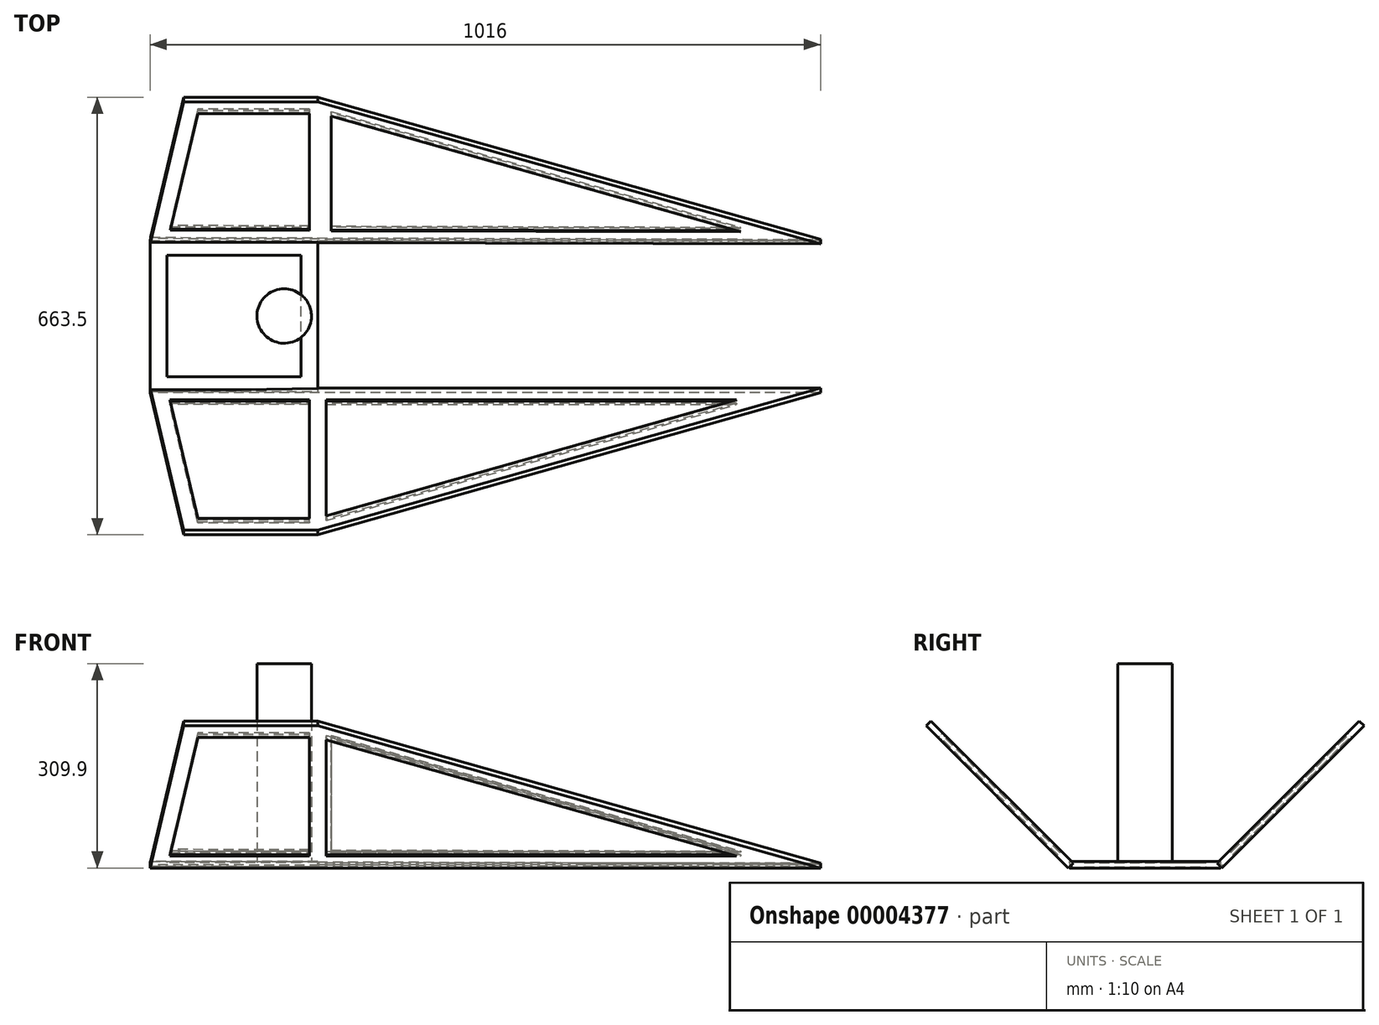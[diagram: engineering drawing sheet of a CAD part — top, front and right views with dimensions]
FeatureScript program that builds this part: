
annotation { "Feature Type Name" : "Feature", "Feature Type Description" : "" }
export const myFeature = defineFeature(function(context is Context, id is Id, definition is map)
    precondition{}
    {
        {
            var Q0;
            Q0=qCreatedBy(makeId("Top.planeOp"),FACE);
            var sketch = newSketch(context, id + "F0", { "sketchPlane" : qUnion([Q0])});
            skLineSegment(sketch, "E0.rect.bottom", {"start": v(-127, 114.3) * mm, "end": v(127, 114.3) * mm});
            skLineSegment(sketch, "E0.rect.top", {"start": v(-127, -114.3) * mm, "end": v(127, -114.3) * mm});
            skLineSegment(sketch, "E0.rect.left", {"start": v(-127, 114.3) * mm, "end": v(-127, -114.3) * mm});
            skLineSegment(sketch, "E0.rect.right", {"start": v(127, 114.3) * mm, "end": v(127, -114.3) * mm});
            skPoint(sketch, "E0.rect.middle", {"position": v(0, 0) * mm});
            skSolve(sketch);
        }
        {
            var Q0;
            Q0=makeQuery(id+"F0.imprint","IMPRINT",FACE,{"disambiguationData":[TD([[makeQuery(id+"F0.imprint","IMPRINT",EDGE,{"derivedFrom":sQuery(id+"F0.wireOp",EDGE,"E0.rect.bottom")}),-1.0]])]});
            extrude(context, id + "F1", {"entities" : qUnion([Q0]), "endBound" : BoundingType.SYMMETRIC, "depth" : 6.35 * mm});
        }
        {
            var Q0;
            Q0=makeQuery(id+"F1.opExtrude","CAP_EDGE",EDGE,{"disambiguationData":[OSD([sQuery(id+"F0.wireOp",EDGE,"E0.rect.top")])],"isStart":true});
            cPlane(context, id + "F2", {"entities" : qUnion([Q0]), "cplaneType" : CPlaneType.LINE_ANGLE, "offset" : 152.4 * mm, "angle" : 45 * degree, "width" : 152.4 * mm, "height" : 152.4 * mm});
        }
        {
            var Q0;
            Q0=qCreatedBy(id+"F2.planeOp",FACE);
            var sketch = newSketch(context, id + "F3", { "sketchPlane" : qUnion([Q0])});
            skLineSegment(sketch, "E1.0", {"start": v(127, 78.58) * mm, "end": v(-127, 78.58) * mm});
            skLineSegment(sketch, "E2", {"start": v(-127, 78.58) * mm, "end": v(-127, 383.38) * mm});
            skLineSegment(sketch, "E3", {"start": v(-127, 383.38) * mm, "end": v(76.2, 383.38) * mm});
            skLineSegment(sketch, "E4", {"start": v(127, 78.58) * mm, "end": v(76.2, 383.38) * mm});
            skSolve(sketch);
        }
        {
            var Q0;
            Q0=makeQuery(id+"F3.imprint","IMPRINT",FACE,{"disambiguationData":[TD([[makeQuery(id+"F3.imprint","IMPRINT",EDGE,{"derivedFrom":sQuery(id+"F3.wireOp",EDGE,"E1.0")}),-1.0]])]});
            extrude(context, id + "F4", {"entities" : qUnion([Q0]), "operationType" : NewBodyOperationType.ADD, "depth" : 4.72 * mm});
        }
        {
            var Q0;
            Q0=makeQuery(id+"F1.opExtrude","CAP_EDGE",EDGE,{"disambiguationData":[OSD([sQuery(id+"F0.wireOp",EDGE,"E0.rect.bottom")])],"isStart":true});
            cPlane(context, id + "F5", {"entities" : qUnion([Q0]), "cplaneType" : CPlaneType.LINE_ANGLE, "offset" : 152.4 * mm, "angle" : 135 * degree, "width" : 152.4 * mm, "height" : 152.4 * mm});
        }
        {
            var Q0;
            Q0=qCreatedBy(id+"F5.planeOp",FACE);
            var sketch = newSketch(context, id + "F6", { "sketchPlane" : qUnion([Q0])});
            skLineSegment(sketch, "E5.0", {"start": v(-127, 78.58) * mm, "end": v(127, 78.58) * mm});
            skLineSegment(sketch, "E6", {"start": v(127, 78.58) * mm, "end": v(127, 383.38) * mm});
            skLineSegment(sketch, "E7.0", {"start": v(127, -83.07) * mm, "end": v(-76.2, -83.07) * mm, "construction": true});
            skLineSegment(sketch, "E8", {"start": v(127, 383.38) * mm, "end": v(-76.2, 383.38) * mm});
            skLineSegment(sketch, "E9", {"start": v(-76.2, 383.38) * mm, "end": v(-127, 78.58) * mm});
            skSolve(sketch);
        }
        {
            var Q0;
            Q0=makeQuery(id+"F6.imprint","IMPRINT",FACE,{"disambiguationData":[TD([[makeQuery(id+"F6.imprint","IMPRINT",EDGE,{"derivedFrom":sQuery(id+"F6.wireOp",EDGE,"E5.0")}),1.0]])]});
            extrude(context, id + "F7", {"entities" : qUnion([Q0]), "operationType" : NewBodyOperationType.ADD, "depth" : 4.72 * mm});
        }
        {
            var Q0;
            Q0=qCreatedBy(id+"F2.planeOp",FACE);
            var sketch = newSketch(context, id + "F8", { "sketchPlane" : qUnion([Q0])});
            skLineSegment(sketch, "E10.0", {"start": v(-127, 78.58) * mm, "end": v(-127, 383.38) * mm});
            skLineSegment(sketch, "E11", {"start": v(-127, 78.58) * mm, "end": v(-889, 78.58) * mm});
            skLineSegment(sketch, "E12", {"start": v(-889, 78.58) * mm, "end": v(-127, 383.38) * mm});
            skSolve(sketch);
        }
        {
            var Q0;
            Q0=makeQuery(id+"F8.imprint","IMPRINT",FACE,{"disambiguationData":[TD([[makeQuery(id+"F8.imprint","IMPRINT",EDGE,{"derivedFrom":sQuery(id+"F8.wireOp",EDGE,"E10.0")}),1.0]])]});
            extrude(context, id + "F9", {"entities" : qUnion([Q0]), "operationType" : NewBodyOperationType.ADD, "depth" : 4.72 * mm});
        }
        {
            var Q0;
            Q0=qCreatedBy(id+"F5.planeOp",FACE);
            var sketch = newSketch(context, id + "F10", { "sketchPlane" : qUnion([Q0])});
            skLineSegment(sketch, "E13.0", {"start": v(127, 78.58) * mm, "end": v(127, 383.38) * mm});
            skLineSegment(sketch, "E14", {"start": v(127, 78.58) * mm, "end": v(889, 78.58) * mm});
            skLineSegment(sketch, "E15", {"start": v(889, 78.58) * mm, "end": v(127, 383.38) * mm});
            skSolve(sketch);
        }
        {
            var Q0;
            Q0=makeQuery(id+"F10.imprint","IMPRINT",FACE,{"disambiguationData":[TD([[makeQuery(id+"F10.imprint","IMPRINT",EDGE,{"derivedFrom":sQuery(id+"F10.wireOp",EDGE,"E13.0")}),-1.0]])]});
            extrude(context, id + "F11", {"entities" : qUnion([Q0]), "operationType" : NewBodyOperationType.ADD, "depth" : 4.72 * mm});
        }
        {
            var Q0;
            Q0=makeQuery(id+"F9.boolean.opBoolean","MERGE",FACE,{"derivedFrom":[makeQuery(id+"F4.opExtrude","CAP_FACE",FACE,{"disambiguationData":[OSD([sQuery(id+"F3.wireOp",EDGE,"E1.0"),sQuery(id+"F3.wireOp",EDGE,"E2"),sQuery(id+"F3.wireOp",EDGE,"E3"),sQuery(id+"F3.wireOp",EDGE,"E4")])],"isStart":false}),makeQuery(id+"F9.opExtrude","CAP_FACE",FACE,{"disambiguationData":[OSD([sQuery(id+"F8.wireOp",EDGE,"E10.0"),sQuery(id+"F8.wireOp",EDGE,"E11"),sQuery(id+"F8.wireOp",EDGE,"E12")])],"isStart":false})]});
            cPlane(context, id + "F12", {"entities" : qUnion([Q0]), "cplaneType" : CPlaneType.OFFSET, "offset" : 2.36 * mm, "oppositeDirection" : true, "width" : 152.4 * mm, "height" : 152.4 * mm});
        }
        {
            var Q0;
            Q0=qCreatedBy(id+"F12.planeOp",FACE);
            var sketch = newSketch(context, id + "F13", { "sketchPlane" : qUnion([Q0])});
            skLineSegment(sketch, "E16.0", {"start": v(-889, 78.58) * mm, "end": v(-127, 383.38) * mm});
            skLineSegment(sketch, "E17.0", {"start": v(-127, 383.38) * mm, "end": v(76.2, 383.38) * mm});
            skLineSegment(sketch, "E18.0", {"start": v(127, 78.58) * mm, "end": v(76.2, 383.38) * mm});
            skLineSegment(sketch, "E19", {"start": v(-889, 78.58) * mm, "end": v(127, 78.58) * mm});
            skLineSegment(sketch, "E20", {"start": v(-139.7, 352.8) * mm, "end": v(-761.76, 103.98) * mm});
            skLineSegment(sketch, "E21", {"start": v(-139.7, 103.98) * mm, "end": v(-761.76, 103.98) * mm});
            skLineSegment(sketch, "E22", {"start": v(-114.3, 357.98) * mm, "end": v(54.68, 357.98) * mm});
            skLineSegment(sketch, "E23", {"start": v(54.68, 357.98) * mm, "end": v(97.02, 103.98) * mm});
            skLineSegment(sketch, "E24", {"start": v(-114.3, 103.98) * mm, "end": v(97.02, 103.98) * mm});
            skLineSegment(sketch, "E25", {"start": v(-114.3, 357.98) * mm, "end": v(-114.3, 103.98) * mm});
            skLineSegment(sketch, "E26", {"start": v(-139.7, 352.8) * mm, "end": v(-139.7, 103.98) * mm});
            skSolve(sketch);
        }
        {
            var Q0;
            Q0=makeQuery(id+"F13.imprint","IMPRINT",FACE,{"disambiguationData":[TD([[makeQuery(id+"F13.imprint","IMPRINT",EDGE,{"derivedFrom":sQuery(id+"F13.wireOp",EDGE,"E16.0")}),-1.0]])]});
            extrude(context, id + "F14", {"entities" : qUnion([Q0]), "operationType" : NewBodyOperationType.ADD, "endBound" : BoundingType.SYMMETRIC, "depth" : 10.16 * mm});
        }
        {
            var Q0;
            Q0=makeQuery(id+"F11.boolean.opBoolean","MERGE",FACE,{"derivedFrom":[makeQuery(id+"F7.opExtrude","CAP_FACE",FACE,{"disambiguationData":[OSD([sQuery(id+"F6.wireOp",EDGE,"E5.0"),sQuery(id+"F6.wireOp",EDGE,"E6"),sQuery(id+"F6.wireOp",EDGE,"E8"),sQuery(id+"F6.wireOp",EDGE,"E9")])],"isStart":false}),makeQuery(id+"F11.opExtrude","CAP_FACE",FACE,{"disambiguationData":[OSD([sQuery(id+"F10.wireOp",EDGE,"E13.0"),sQuery(id+"F10.wireOp",EDGE,"E14"),sQuery(id+"F10.wireOp",EDGE,"E15")])],"isStart":false})]});
            cPlane(context, id + "F15", {"entities" : qUnion([Q0]), "cplaneType" : CPlaneType.OFFSET, "offset" : 2.36 * mm, "oppositeDirection" : true, "width" : 152.4 * mm, "height" : 152.4 * mm});
        }
        {
            var Q0;
            Q0=qCreatedBy(id+"F15.planeOp",FACE);
            var sketch = newSketch(context, id + "F16", { "sketchPlane" : qUnion([Q0])});
            skLineSegment(sketch, "E27.0", {"start": v(-76.2, 383.38) * mm, "end": v(-126.3, 82.83) * mm});
            skLineSegment(sketch, "E28.0", {"start": v(127, 383.38) * mm, "end": v(-76.2, 383.38) * mm});
            skLineSegment(sketch, "E29.0", {"start": v(889, 78.58) * mm, "end": v(127, 383.38) * mm});
            skLineSegment(sketch, "E30", {"start": v(-126.3, 82.83) * mm, "end": v(889, 78.58) * mm});
            skLineSegment(sketch, "E31", {"start": v(147.15, 107.12) * mm, "end": v(768.1, 104.52) * mm});
            skLineSegment(sketch, "E32", {"start": v(147.15, 352.9) * mm, "end": v(768.1, 104.52) * mm});
            skLineSegment(sketch, "E33", {"start": v(114.3, 357.98) * mm, "end": v(-54.68, 357.98) * mm});
            skLineSegment(sketch, "E34", {"start": v(-54.68, 357.98) * mm, "end": v(-96.32, 108.14) * mm});
            skLineSegment(sketch, "E35", {"start": v(114.3, 107.26) * mm, "end": v(-96.32, 108.14) * mm});
            skLineSegment(sketch, "E36", {"start": v(114.3, 357.98) * mm, "end": v(114.3, 107.26) * mm});
            skLineSegment(sketch, "E37", {"start": v(147.15, 352.9) * mm, "end": v(147.15, 107.12) * mm});
            skPoint(sketch, "E38.orphan", {"position": v(134.45, 357.98) * mm});
            skSolve(sketch);
        }
        {
            var Q0;
            Q0=makeQuery(id+"F16.imprint","IMPRINT",FACE,{"disambiguationData":[TD([[makeQuery(id+"F16.imprint","IMPRINT",EDGE,{"derivedFrom":sQuery(id+"F16.wireOp",EDGE,"E27.0")}),1.0]])]});
            extrude(context, id + "F17", {"entities" : qUnion([Q0]), "operationType" : NewBodyOperationType.ADD, "endBound" : BoundingType.SYMMETRIC, "depth" : 10.16 * mm});
        }
        {
            var Q0;
            Q0=qCreatedBy(makeId("Top.planeOp"),FACE);
            var sketch = newSketch(context, id + "F18", { "sketchPlane" : qUnion([Q0])});
            skLineSegment(sketch, "E39.0", {"start": v(-127, 114.3) * mm, "end": v(-127, -114.3) * mm});
            skLineSegment(sketch, "E40.0", {"start": v(127, 112.47) * mm, "end": v(127, -110.13) * mm});
            skLineSegment(sketch, "E41", {"start": v(-127, -114.3) * mm, "end": v(127, -110.13) * mm});
            skLineSegment(sketch, "E42", {"start": v(127, 112.47) * mm, "end": v(-127, 114.3) * mm});
            skLineSegment(sketch, "E43.rect.bottom", {"start": v(-101.6, 92.3) * mm, "end": v(101.6, 92.3) * mm});
            skLineSegment(sketch, "E43.rect.top", {"start": v(-101.6, -92.3) * mm, "end": v(101.6, -92.3) * mm});
            skLineSegment(sketch, "E43.rect.left", {"start": v(-101.6, 92.3) * mm, "end": v(-101.6, -92.3) * mm});
            skLineSegment(sketch, "E43.rect.right", {"start": v(101.6, 92.3) * mm, "end": v(101.6, -92.3) * mm});
            skPoint(sketch, "E43.rect.middle", {"position": v(0, 0) * mm});
            skSolve(sketch);
        }
        {
            var Q0;
            Q0=makeQuery(id+"F18.imprint","IMPRINT",FACE,{"disambiguationData":[TD([[makeQuery(id+"F18.imprint","IMPRINT",EDGE,{"derivedFrom":sQuery(id+"F18.wireOp",EDGE,"E39.0")}),1.0]])]});
            extrude(context, id + "F19", {"entities" : qUnion([Q0]), "operationType" : NewBodyOperationType.ADD, "endBound" : BoundingType.SYMMETRIC, "depth" : 10.16 * mm});
        }
        {
            var Q0;
            Q0=qCreatedBy(makeId("Top.planeOp"),FACE);
            var sketch = newSketch(context, id + "F20", { "sketchPlane" : qUnion([Q0])});
            skCircle(sketch, "E44", {"center": v(76.2, 0) * mm, "radius": 41.27 * mm});
            skSolve(sketch);
        }
        {
            var Q0;
            Q0=makeQuery(id+"F20.imprint","IMPRINT",FACE,{"disambiguationData":[TD([[makeQuery(id+"F20.imprint","IMPRINT",EDGE,{"derivedFrom":sQuery(id+"F20.wireOp",EDGE,"E44")}),1.0]])]});
            var Q1;
            Q1=sQuery(id+"F20.wireOp",EDGE,"E44");
            extrude(context, id + "F21", {"entities" : qUnion([Q0]), "operationType" : NewBodyOperationType.ADD, "surfaceEntities" : qUnion([Q1]), "depth" : 304.8 * mm});
        }
    });
